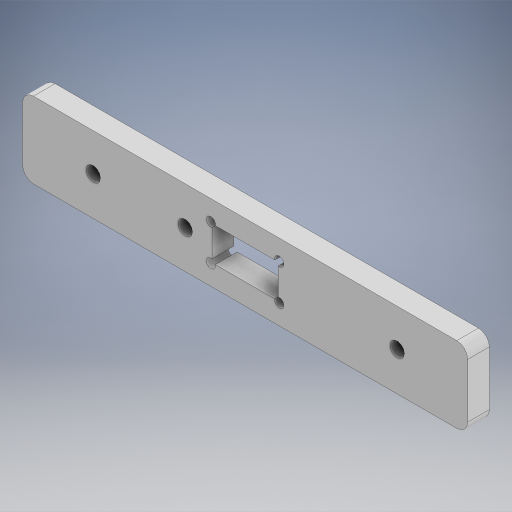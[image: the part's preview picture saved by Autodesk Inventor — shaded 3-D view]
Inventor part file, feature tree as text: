
AUTODESK INVENTOR PART (.ipt)
format: ipt  version: 2024 (Build 280153000, 153)  size: 308,736 bytes
history: native  units: mm
features: other x5, reference x4, extrude x3, sketch x3, fillet x1, projected_geometry x1
ambient origin geometry x8: Origin, YZ Plane, XZ Plane, XY Plane, X Axis, Y Axis, Z Axis, Center Point
bodies: Body1 (feature_tree)
feature tree (17):
  other  "솔리드1"
  other  "작업 평면1"
  extrude  "돌출1"  Depth=0.3mm
  extrude  "돌출2"  Depth=4.0mm
  fillet  "모깎기1"  Radius=4.0mm
  extrude  "돌출3"  Depth=2.1mm
  sketch  "스케치1"
  reference  "참조1"
  reference  "참조2"
  reference  "참조3"
  sketch  "스케치2"
  reference  "참조4"
  sketch  "스케치3"
  projected_geometry  "투영된 루프1"
  other  "<userpath>\Desktop\ZIG\조립품1.iam"
  other  "조립품1.iam"
  other  "head_cover:1"
